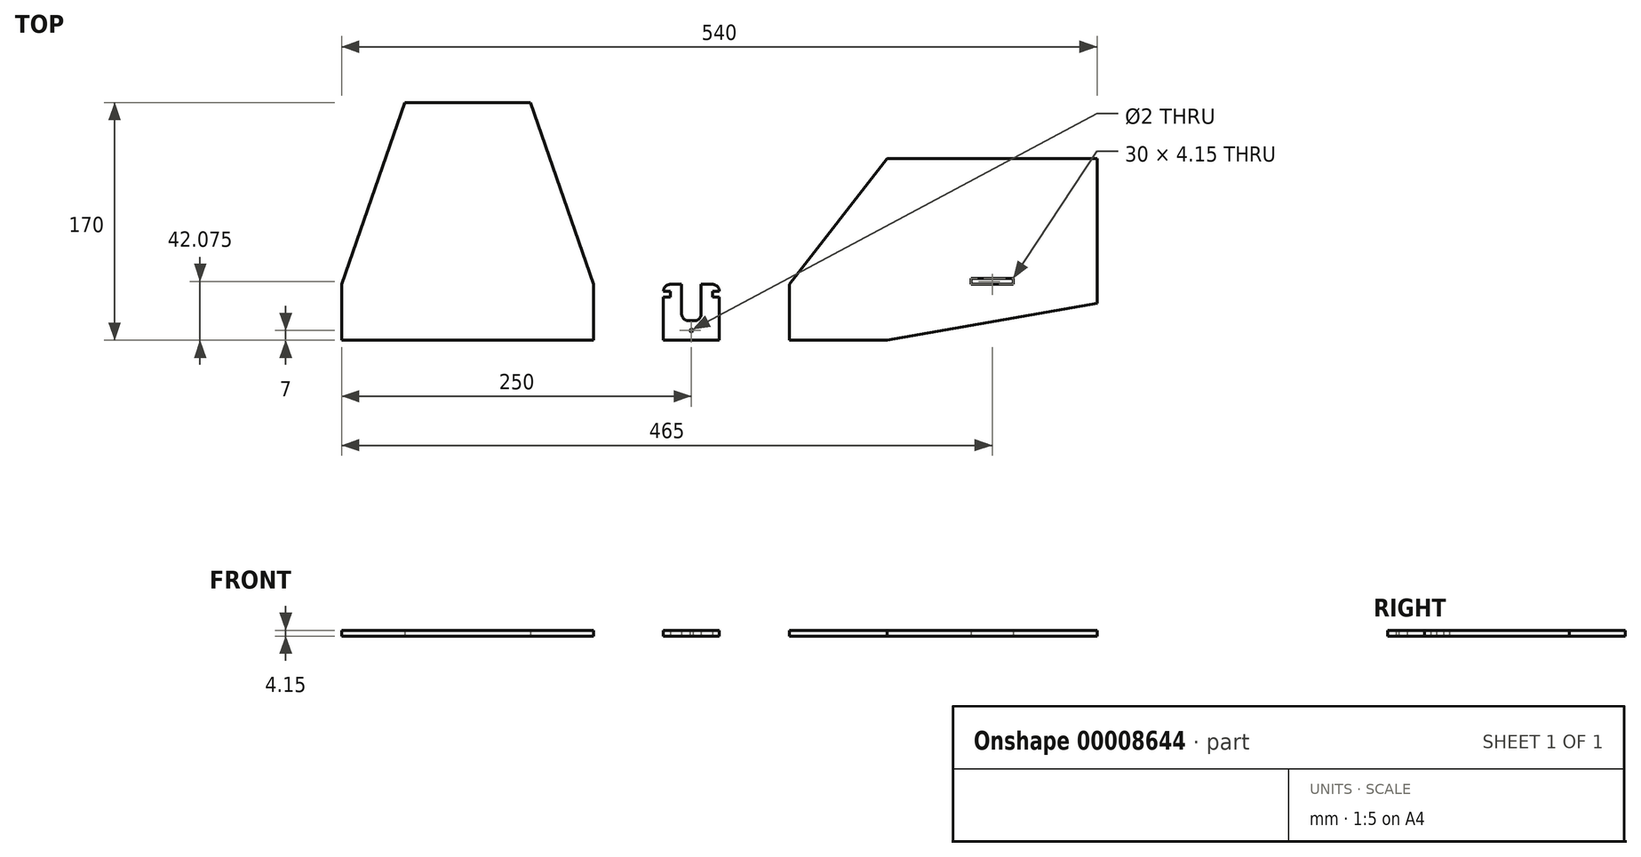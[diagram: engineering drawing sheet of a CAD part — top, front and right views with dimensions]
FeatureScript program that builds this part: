
annotation { "Feature Type Name" : "Feature", "Feature Type Description" : "" }
export const myFeature = defineFeature(function(context is Context, id is Id, definition is map)
    precondition{}
    {
        {
            var Q0;
            Q0=qCreatedBy(makeId("Top.planeOp"),FACE);
            var sketch = newSketch(context, id + "F0", { "sketchPlane" : qUnion([Q0])});
            skLineSegment(sketch, "E0", {"start": v(0, 0) * mm, "end": v(0, 40) * mm});
            skLineSegment(sketch, "E1", {"start": v(70, 130) * mm, "end": v(70, 0) * mm});
            skLineSegment(sketch, "E2", {"start": v(70, 0) * mm, "end": v(0, 0) * mm});
            skLineSegment(sketch, "E3", {"start": v(70, 130) * mm, "end": v(220, 130) * mm});
            skLineSegment(sketch, "E4", {"start": v(220, 130) * mm, "end": v(220, 26.45) * mm});
            skLineSegment(sketch, "E5", {"start": v(220, 26.45) * mm, "end": v(70, 0) * mm});
            skLineSegment(sketch, "E6", {"start": v(-90, 35) * mm, "end": v(-90, 35) * mm});
            skLineSegment(sketch, "E7", {"start": v(-90, 0) * mm, "end": v(-50, 0) * mm});
            skLineSegment(sketch, "E8", {"start": v(-50, 0) * mm, "end": v(-50, 30.85) * mm});
            skLineSegment(sketch, "E9", {"start": v(-55, 40) * mm, "end": v(-63, 40) * mm});
            skLineSegment(sketch, "E10", {"start": v(-63, 40) * mm, "end": v(-63, 19) * mm});
            skLineSegment(sketch, "E11", {"start": v(-68, 14) * mm, "end": v(-72, 14) * mm});
            skLineSegment(sketch, "E12", {"start": v(-77, 19) * mm, "end": v(-77, 40) * mm});
            skLineSegment(sketch, "E13", {"start": v(-77, 40) * mm, "end": v(-85, 40) * mm});
            skLineSegment(sketch, "E14.trimOffspring", {"start": v(-90, 30.85) * mm, "end": v(-90, 0) * mm});
            skLineSegment(sketch, "E15.trimOffspring", {"start": v(-50, 35) * mm, "end": v(-50, 35) * mm});
            skLineSegment(sketch, "E16", {"start": v(-56.5, 40) * mm, "end": v(-56.5, 0) * mm, "construction": true});
            skLineSegment(sketch, "E17", {"start": v(130, 44.15) * mm, "end": v(130, 40) * mm});
            skLineSegment(sketch, "E18", {"start": v(130, 40) * mm, "end": v(160, 40) * mm});
            skLineSegment(sketch, "E19", {"start": v(160, 40) * mm, "end": v(160, 44.15) * mm});
            skLineSegment(sketch, "E20", {"start": v(160, 44.15) * mm, "end": v(130, 44.15) * mm});
            skPoint(sketch, "E21", {"position": v(145, 44.15) * mm});
            skLineSegment(sketch, "E22", {"start": v(145, 44.15) * mm, "end": v(145, 130) * mm, "construction": true});
            skLineSegment(sketch, "E23", {"start": v(-90, 35) * mm, "end": v(-85, 35) * mm});
            skLineSegment(sketch, "E24", {"start": v(-85, 35) * mm, "end": v(-85, 30.85) * mm});
            skLineSegment(sketch, "E25", {"start": v(-85, 30.85) * mm, "end": v(-90, 30.85) * mm});
            skLineSegment(sketch, "E26", {"start": v(-50, 30.85) * mm, "end": v(-55, 30.85) * mm});
            skLineSegment(sketch, "E27", {"start": v(-55, 30.85) * mm, "end": v(-55, 35) * mm});
            skLineSegment(sketch, "E28", {"start": v(-55, 35) * mm, "end": v(-50, 35) * mm});
            skLineSegment(sketch, "E29", {"start": v(-85, 35) * mm, "end": v(-85, 40) * mm, "construction": true});
            skPoint(sketch, "E30.visualSharp", {"position": v(-90, 40) * mm});
            skArc(sketch, "E30.filletArc", {"start": v(-85, 40) * mm, "mid": v(-88.54, 38.54) * mm, "end": v(-90, 35) * mm});
            skPoint(sketch, "E31.visualSharp", {"position": v(-50, 40) * mm});
            skArc(sketch, "E31.filletArc", {"start": v(-50, 35) * mm, "mid": v(-51.46, 38.54) * mm, "end": v(-55, 40) * mm});
            skPoint(sketch, "E32.visualSharp", {"position": v(-77, 14) * mm});
            skArc(sketch, "E32.filletArc", {"start": v(-77, 19) * mm, "mid": v(-75.54, 15.46) * mm, "end": v(-72, 14) * mm});
            skPoint(sketch, "E33.visualSharp", {"position": v(-63, 14) * mm});
            skArc(sketch, "E33.filletArc", {"start": v(-68, 14) * mm, "mid": v(-64.46, 15.46) * mm, "end": v(-63, 19) * mm});
            skPoint(sketch, "E34", {"position": v(-70, 0) * mm});
            skCircle(sketch, "E35", {"center": v(-70, 7) * mm, "radius": 1 * mm});
            skLineSegment(sketch, "E36", {"start": v(-70, 7) * mm, "end": v(-70, 14) * mm, "construction": true});
            skLineSegment(sketch, "E37", {"start": v(-70, 7) * mm, "end": v(-70, 0) * mm, "construction": true});
            skLineSegment(sketch, "E38", {"start": v(70, 0) * mm, "end": v(145, 0) * mm, "construction": true});
            skLineSegment(sketch, "E39", {"start": v(145, 40) * mm, "end": v(145, 0) * mm, "construction": true});
            skLineSegment(sketch, "E40", {"start": v(-50, 0) * mm, "end": v(0, 0) * mm, "construction": true});
            skLineSegment(sketch, "E41", {"start": v(70, 130) * mm, "end": v(0, 40) * mm});
            skLineSegment(sketch, "E42", {"start": v(-250, 40) * mm, "end": v(-250, 0) * mm});
            skLineSegment(sketch, "E43", {"start": v(-210, 40) * mm, "end": v(-210, 0) * mm});
            skLineSegment(sketch, "E44", {"start": v(-320, 0) * mm, "end": v(-140, 0) * mm});
            skLineSegment(sketch, "E45", {"start": v(-140, 0) * mm, "end": v(-140, 40) * mm});
            skLineSegment(sketch, "E46", {"start": v(-320, 40) * mm, "end": v(-320, 0) * mm});
            skLineSegment(sketch, "E47", {"start": v(-320, 40) * mm, "end": v(-250, 40) * mm});
            skLineSegment(sketch, "E48", {"start": v(-210, 40) * mm, "end": v(-140, 40) * mm});
            skLineSegment(sketch, "E49", {"start": v(-210, 40) * mm, "end": v(-250, 40) * mm});
            skLineSegment(sketch, "E50", {"start": v(-250, 170) * mm, "end": v(-210, 170) * mm});
            skLineSegment(sketch, "E51", {"start": v(-210, 170) * mm, "end": v(-210, 40) * mm});
            skLineSegment(sketch, "E52", {"start": v(-250, 40) * mm, "end": v(-250, 170) * mm});
            skLineSegment(sketch, "E53", {"start": v(-140, 0) * mm, "end": v(-90, 0) * mm, "construction": true});
            skLineSegment(sketch, "E54", {"start": v(-210, 170) * mm, "end": v(-185, 170) * mm});
            skLineSegment(sketch, "E55", {"start": v(-185, 170) * mm, "end": v(-140, 40) * mm});
            skLineSegment(sketch, "E56", {"start": v(-250, 170) * mm, "end": v(-275, 170) * mm});
            skLineSegment(sketch, "E57", {"start": v(-275, 170) * mm, "end": v(-320, 40) * mm});
            skLineSegment(sketch, "E58", {"start": v(-77, 40) * mm, "end": v(-63, 40) * mm});
            skSolve(sketch);
        }
        {
            var Q0;
            {var subQ2=sQuery(id+"F0.wireOp",EDGE,"E42");Q0=makeQuery(id+"F0.imprint","IMPRINT",FACE,{"disambiguationData":[TD([[makeQuery(id+"F0.imprint","IMPRINT",EDGE,{"derivedFrom":subQ2}),-1.0]])]});}
            var Q1;
            Q1=makeQuery(id+"F0.imprint","IMPRINT",FACE,{"disambiguationData":[TD([[makeQuery(id+"F0.imprint","IMPRINT",EDGE,{"derivedFrom":sQuery(id+"F0.wireOp",EDGE,"E1")}),1.0]])]});
            var Q2;
            Q2=makeQuery(id+"F0.imprint","IMPRINT",FACE,{"disambiguationData":[TD([[makeQuery(id+"F0.imprint","IMPRINT",EDGE,{"derivedFrom":sQuery(id+"F0.wireOp",EDGE,"E7")}),1.0]])]});
            var Q3;
            Q3=makeQuery(id+"F0.imprint","IMPRINT",FACE,{"disambiguationData":[TD([[makeQuery(id+"F0.imprint","IMPRINT",EDGE,{"derivedFrom":sQuery(id+"F0.wireOp",EDGE,"E0")}),-1.0]])]});
            var Q4;
            Q4=makeQuery(id+"F0.imprint","IMPRINT",FACE,{"disambiguationData":[TD([[makeQuery(id+"F0.imprint","IMPRINT",EDGE,{"derivedFrom":sQuery(id+"F0.wireOp",EDGE,"E49")}),-1.0]])]});
            var Q5;
            {var subQ2=sQuery(id+"F0.wireOp",EDGE,"E42");Q5=makeQuery(id+"F0.imprint","IMPRINT",FACE,{"disambiguationData":[TD([[makeQuery(id+"F0.imprint","IMPRINT",EDGE,{"derivedFrom":subQ2}),1.0]])]});}
            var Q6;
            Q6=makeQuery(id+"F0.imprint","IMPRINT",FACE,{"disambiguationData":[TD([[makeQuery(id+"F0.imprint","IMPRINT",EDGE,{"derivedFrom":sQuery(id+"F0.wireOp",EDGE,"E48")}),1.0]])]});
            var Q7;
            {var subQ2=sQuery(id+"F0.wireOp",EDGE,"E43");Q7=makeQuery(id+"F0.imprint","IMPRINT",FACE,{"disambiguationData":[TD([[makeQuery(id+"F0.imprint","IMPRINT",EDGE,{"derivedFrom":subQ2}),1.0]])]});}
            var Q8;
            Q8=makeQuery(id+"F0.imprint","IMPRINT",FACE,{"disambiguationData":[TD([[makeQuery(id+"F0.imprint","IMPRINT",EDGE,{"derivedFrom":sQuery(id+"F0.wireOp",EDGE,"E47")}),1.0]])]});
            extrude(context, id + "F1", {"entities" : qUnion([Q0, Q1, Q2, Q3, Q4, Q5, Q6, Q7, Q8]), "depth" : 4.15 * mm});
        }
    });
